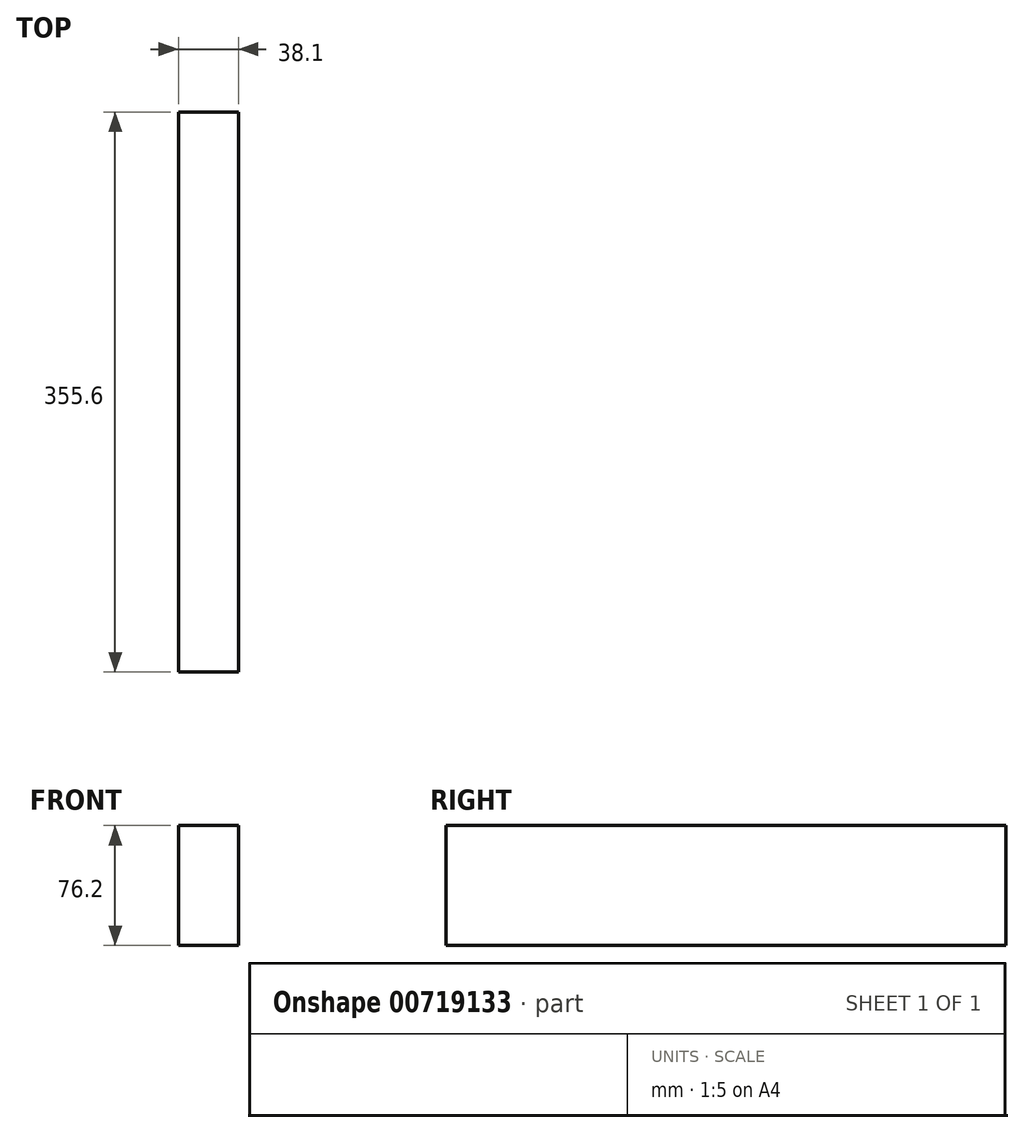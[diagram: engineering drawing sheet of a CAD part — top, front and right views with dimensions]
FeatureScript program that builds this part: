
annotation { "Feature Type Name" : "Feature", "Feature Type Description" : "" }
export const myFeature = defineFeature(function(context is Context, id is Id, definition is map)
    precondition{}
    {
        {
            var Q0;
            Q0=qCreatedBy(makeId("Front.planeOp"),FACE);
            var sketch = newSketch(context, id + "F0", { "sketchPlane" : qUnion([Q0])});
            skLineSegment(sketch, "E0.bottom", {"start": v(0, 0) * mm, "end": v(-38.1, 0) * mm});
            skLineSegment(sketch, "E0.top", {"start": v(0, 76.2) * mm, "end": v(-38.1, 76.2) * mm});
            skLineSegment(sketch, "E0.left", {"start": v(0, 0) * mm, "end": v(0, 76.2) * mm});
            skLineSegment(sketch, "E0.right", {"start": v(-38.1, 0) * mm, "end": v(-38.1, 76.2) * mm});
            skSolve(sketch);
        }
        {
            var Q0;
            Q0 = qSketchRegion(id + "F0", true);
            extrude(context, id + "F1", {"entities" : qUnion([Q0]), "depth" : 355.6 * mm, "offsetDistance" : 25.4 * mm});
        }
    });
